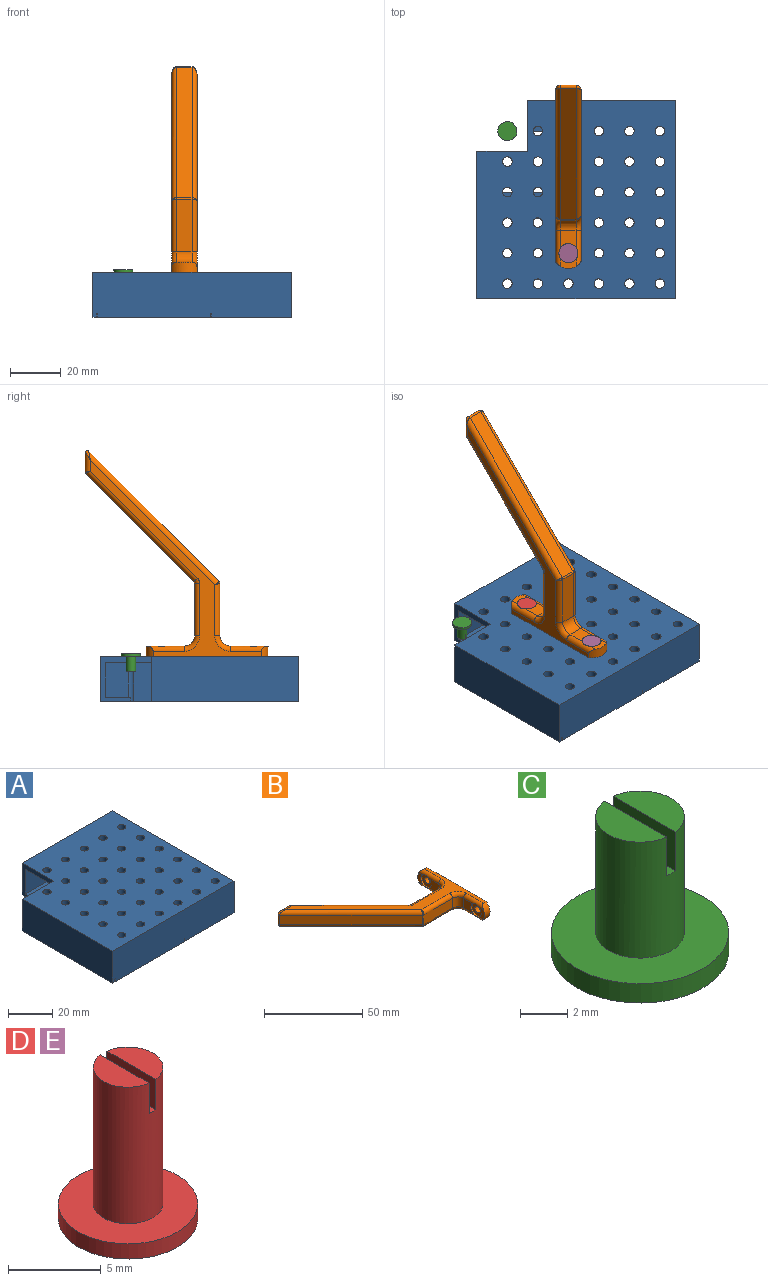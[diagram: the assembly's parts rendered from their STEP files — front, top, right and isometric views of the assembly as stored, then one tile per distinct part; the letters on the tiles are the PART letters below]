
ASSEMBLY  parts=5 mates=4
PART A: 73 faces, bbox 78x78x17.8 mm
  f0: plane 11.33x1.5mm, normal (1,0,0), area 17mm2, adj f6,f15,f25,f26,f48
  f1: plane 10.65x1.5mm, normal (1,0,0), area 16mm2, adj f6,f14,f46,f48
  f2: plane 10.65x1.5mm, normal (1,0,0), area 16mm2, adj f6,f17,f46,f47
  f3: plane 5.33x1.5mm, normal (1,0,0), area 8mm2, adj f6,f16,f45,f47
  f4: plane 45x44mm, normal (0,0,-1), area 1556.9mm2, adj f7,f8,f9,f13,f24,f28,f29,f30
  f5: plane 78x31.5mm, normal (0,0,-1), area 2261.6mm2, adj f7,f8,f9,f10,f11,f12,f13,f27
  f6: plane 44.5x42mm, normal (0,0,-1), area 1769.3mm2, adj f0,f1,f2,f3,f25,f39,f45,f46
  f7: plane 15.25x9.75mm, normal (-1,0,0), area 148.7mm2, adj f4,f5,f50,f51
  f8: plane 15.25x9.75mm, normal (-1,0,0), area 136.7mm2, adj f4,f5,f15,f37,f48,f51
  f9: plane 15.25x9.75mm, normal (-1,0,0), area 148.7mm2, adj f4,f5,f49,f50
  f10: plane 9.75x1.5mm, normal (-1,0,0), area 14.6mm2, adj f5,f14,f46,f48
  f11: plane 9.75x1.5mm, normal (-1,0,0), area 14.6mm2, adj f5,f17,f46,f47
  f12: plane 4.88x1.5mm, normal (-1,0,0), area 7.3mm2, adj f5,f16,f45,f47
  f13: plane 15.25x10.88mm, normal (-1,0,0), area 138.3mm2, adj f4,f5,f24,f27,f41,f49
  f14: plane 10.65x0.25mm, normal (0,0,-1), area 2.5mm2, adj f1,f10,f46,f48
  f15: plane 1.33x0.25mm, normal (0,0,-1), area 0.3mm2, adj f0,f8,f37,f48
  f16: plane 5.33x0.25mm, normal (0,0,-1), area 1.3mm2, adj f3,f12,f45,f47
  f17: plane 10.65x0.25mm, normal (0,0,-1), area 2.5mm2, adj f2,f11,f46,f47
  f18: plane 58x1.5mm, normal (0,0,-1), area 87mm2, adj f20,f36,f43,f45
  f19: plane 26.25x12mm, normal (0,0,-1), area 315mm2, adj f21,f27,f40,f42
  f20: plane 58x17.75mm, normal (-1,0,0), area 1029.5mm2, adj f18,f23,f43,f45
  f21: plane 26.25x1.5mm, normal (0,-1,0), area 39.4mm2, adj f19,f22,f40,f42
  f22: plane 26.25x10mm, normal (0,0,1), area 262.5mm2, adj f21,f24,f40,f42
  f23: plane 78x78mm, normal (0,0,1), area 5297.4mm2, adj f20,f27,f28,f29,f30,f31,f32,f33
  f24: plane 26.5x13.75mm, normal (0,-1,0), area 364.4mm2, adj f4,f13,f22,f41,f42
  f25: plane 44.5x1.5mm, normal (0,1,0), area 66.7mm2, adj f0,f6,f26,f39
  f26: plane 44.5x10mm, normal (0,0,1), area 445mm2, adj f0,f25,f37,f39
  f27: plane 58x17.75mm, normal (0,1,0), area 1029.1mm2, adj f5,f13,f19,f23,f40,f41,f42,f44
  f28: cylinder r=1.88mm len=3.75mm, axis (0,0,-1), area 29.5mm2, adj f4,f23
  f29: cylinder r=1.88mm len=3.75mm, axis (0,0,-1), area 29.5mm2, adj f4,f23
  f30: cylinder r=1.88mm len=3.75mm, axis (0,0,-1), area 29.5mm2, adj f4,f23
  f31: cylinder r=1.88mm len=3.75mm, axis (0,0,-1), area 29.5mm2, adj f4,f23
  f32: cylinder r=1.88mm len=3.75mm, axis (0,0,-1), area 29.5mm2, adj f4,f23
  f33: cylinder r=1.88mm len=3.75mm, axis (0,0,-1), area 29.5mm2, adj f4,f23
  f34: cylinder r=1.88mm len=3.75mm, axis (0,0,-1), area 29.5mm2, adj f4,f23
  f35: cylinder r=1.88mm len=3.75mm, axis (0,0,-1), area 29.5mm2, adj f4,f23
  f36: plane 58x15.25mm, normal (1,0,0), area 444.5mm2, adj f4,f18,f37,f38,f43,f45
  f37: plane 45x13.75mm, normal (0,1,0), area 618.8mm2, adj f4,f8,f15,f26,f36,f38
  f38: plane 32x0.25mm, normal (0,0,-1), area 8mm2, adj f36,f37,f39,f45
  f39: plane 42x1.5mm, normal (-1,0,0), area 63mm2, adj f6,f25,f26,f38,f45
  f40: plane 12x1.5mm, normal (1,0,0), area 18mm2, adj f19,f21,f22,f27,f41
  f41: plane 2x0.25mm, normal (0,0,-1), area 0.5mm2, adj f13,f24,f27,f40
  f42: plane 20x17.75mm, normal (-1,0,0), area 95.5mm2, adj f4,f19,f21,f22,f23,f24,f27,f43
  f43: plane 20x17.75mm, normal (0,1,0), area 72.9mm2, adj f4,f18,f20,f23,f36,f42
  f44: plane 78x17.75mm, normal (1,0,0), area 1384.5mm2, adj f5,f23,f27,f45
  f45: plane 78x17.75mm, normal (0,-1,0), area 1383.8mm2, adj f3,f5,f6,f12,f16,f18,f20,f23
  f46: cylinder r=1.88mm len=17.75mm, axis (0,0,1), area 207.6mm2, adj f1,f2,f5,f6,f10,f11,f14,f17
  f47: cylinder r=1.88mm len=17.75mm, axis (0,0,1), area 207.6mm2, adj f2,f3,f5,f6,f11,f12,f16,f17
  f48: cylinder r=1.88mm len=17.75mm, axis (0,0,1), area 207.6mm2, adj f0,f1,f5,f6,f8,f10,f14,f15
  f49: cylinder r=1.88mm len=17.75mm, axis (0,0,1), area 172.3mm2, adj f4,f5,f9,f13,f23
  f50: cylinder r=1.88mm len=17.75mm, axis (0,0,1), area 172.3mm2, adj f4,f5,f7,f9,f23
  f51: cylinder r=1.88mm len=17.75mm, axis (0,0,1), area 172.3mm2, adj f4,f5,f7,f8,f23
  f52: cylinder r=1.88mm len=17.75mm, axis (0,0,1), area 209.1mm2, adj f6,f23
  f53: cylinder r=1.88mm len=17.75mm, axis (0,0,1), area 209.1mm2, adj f6,f23
  f54: cylinder r=1.88mm len=17.75mm, axis (0,0,1), area 209.1mm2, adj f6,f23
  f55: cylinder r=1.88mm len=17.75mm, axis (0,0,1), area 209.1mm2, adj f6,f23
  f56: cylinder r=1.88mm len=17.75mm, axis (0,0,1), area 209.1mm2, adj f6,f23
  f57: cylinder r=1.88mm len=17.75mm, axis (0,0,1), area 209.1mm2, adj f6,f23
  f58: cylinder r=1.88mm len=17.75mm, axis (0,0,1), area 209.1mm2, adj f6,f23
  f59: cylinder r=1.88mm len=17.75mm, axis (0,0,1), area 209.1mm2, adj f6,f23
  f60: cylinder r=1.88mm len=17.75mm, axis (0,0,1), area 209.1mm2, adj f6,f23
  f61: cylinder r=1.88mm len=17.75mm, axis (0,0,1), area 209.1mm2, adj f5,f23
  f62: cylinder r=1.88mm len=17.75mm, axis (0,0,1), area 209.1mm2, adj f5,f23
  f63: cylinder r=1.88mm len=17.75mm, axis (0,0,1), area 209.1mm2, adj f5,f23
  f64: cylinder r=1.88mm len=17.75mm, axis (0,0,1), area 209.1mm2, adj f5,f23
  f65: cylinder r=1.88mm len=17.75mm, axis (0,0,1), area 209.1mm2, adj f5,f23
  f66: cylinder r=1.88mm len=17.75mm, axis (0,0,1), area 209.1mm2, adj f5,f23
  f67: cylinder r=1.88mm len=17.75mm, axis (0,0,1), area 209.1mm2, adj f5,f23
  f68: cylinder r=1.88mm len=17.75mm, axis (0,0,1), area 209.1mm2, adj f5,f23
  f69: cylinder r=1.88mm len=17.75mm, axis (0,0,1), area 209.1mm2, adj f5,f23
  f70: cylinder r=1.88mm len=17.75mm, axis (0,0,1), area 209.1mm2, adj f5,f23
  f71: cylinder r=1.88mm len=17.75mm, axis (0,0,1), area 209.1mm2, adj f5,f23
  f72: cylinder r=1.88mm len=17.75mm, axis (0,0,1), area 209.1mm2, adj f5,f23
PART B: 52 faces, bbox 82x72x10 mm
  f0: plane 6.75x6mm, normal (-1,0,0), area 34.2mm2, adj f8,f34,f47,f49
  f1: plane 6x3.75mm, normal (-1,0,0), area 14.6mm2, adj f21,f34,f47,f49
  f2: plane 6x3.75mm, normal (-1,0,0), area 14.6mm2, adj f20,f22,f35,f50
  f3: plane 6.75x6mm, normal (-1,0,0), area 34.2mm2, adj f9,f22,f35,f50
  f4: cylinder r=1.88mm len=3.75mm, axis (1,0,0), area 35.3mm2, adj f6,f48
  f5: plane 77.17x67.32mm, normal (0,0,1), area 462.7mm2, adj f6,f20,f21,f35,f36,f37,f38,f39
  f6: plane 48x10mm, normal (1,0,0), area 442mm2, adj f4,f5,f7,f19,f20,f21
  f7: plane 77.17x67.32mm, normal (0,0,-1), area 462.7mm2, adj f6,f20,f21,f22,f23,f24,f25,f26
  f8: cylinder r=4mm len=6mm, axis (0,0,-1), area 37.7mm2, adj f0,f18,f33,f46
  f9: cylinder r=4mm len=6mm, axis (0,0,-1), area 37.7mm2, adj f3,f10,f23,f36
  f10: plane 20.67x6mm, normal (0,1,0), area 124mm2, adj f9,f11,f24,f37
  f11: cylinder r=0.81mm len=6mm, axis (0,0,-1), area 3.8mm2, adj f10,f12,f25,f38
  f12: plane 42.53x42.53mm, normal (0.71,0.71,0), area 360.9mm2, adj f11,f13,f26,f39
  f13: cylinder r=0.81mm len=6mm, axis (0,0,-1), area 3.8mm2, adj f12,f14,f27,f40
  f14: plane 7.72x6mm, normal (0,1,0), area 46.3mm2, adj f13,f15,f28,f41
  f15: cylinder r=0.81mm len=6mm, axis (0,0,-1), area 11.4mm2, adj f14,f16,f29,f42
  f16: plane 51.33x51.33mm, normal (-0.71,-0.71,0), area 435.6mm2, adj f15,f17,f30,f43
  f17: cylinder r=1mm len=6mm, axis (0,0,-1), area 4.7mm2, adj f16,f18,f31,f44
  f18: plane 20.59x6mm, normal (0,-1,0), area 123.5mm2, adj f8,f17,f32,f45
  f19: cylinder r=1.88mm len=3.75mm, axis (1,0,0), area 35.3mm2, adj f6,f51
  f20: cylinder r=6mm len=10mm, axis (1,0,0), area 44.6mm2, adj f2,f5,f6,f7,f22,f35
  f21: cylinder r=6mm len=10mm, axis (1,0,0), area 44.6mm2, adj f1,f5,f6,f7,f34,f47
  f22: cylinder r=2mm len=14.2mm, axis (0,-1,0), area 38.9mm2, adj f2,f3,f7,f20,f23,f50
  f23: torus R=6mm, axis (0,0,1), area 23.3mm2, adj f7,f9,f22,f24
  f24: cylinder r=2mm len=20.67mm, axis (-1,0,0), area 64.9mm2, adj f7,f10,f23,f25
  f25: torus R=2.81mm, axis (0,0,1), area 3.8mm2, adj f7,f11,f24,f26
  f26: cylinder r=2mm len=43.94mm, axis (-0.71,0.71,0), area 188.4mm2, adj f7,f12,f25,f27
  f27: bspline ~2.28x2mm, area 1.3mm2, adj f13,f26,f28
  f28: cylinder r=2mm len=7.72mm, axis (-1,0,0), area 20.4mm2, adj f7,f14,f27,f29
  f29: bspline ~4.83x2.82mm, area 4.8mm2, adj f15,f28,f30
  f30: cylinder r=2mm len=52.75mm, axis (0.71,-0.71,0), area 224.3mm2, adj f7,f16,f29,f31
  f31: bspline ~2.28x2mm, area 1.6mm2, adj f17,f30,f32
  f32: cylinder r=2mm len=20.59mm, axis (1,0,0), area 64.2mm2, adj f7,f18,f31,f33
  f33: torus R=6mm, axis (0,0,1), area 23.3mm2, adj f7,f8,f32,f34
  f34: cylinder r=2mm len=14.2mm, axis (0,-1,0), area 38.9mm2, adj f0,f1,f7,f21,f33,f49
  f35: cylinder r=2mm len=14.2mm, axis (0,1,0), area 38.9mm2, adj f2,f3,f5,f20,f36,f50
  f36: torus R=6mm, axis (0,0,1), area 23.3mm2, adj f5,f9,f35,f37
  f37: cylinder r=2mm len=20.67mm, axis (1,0,0), area 64.9mm2, adj f5,f10,f36,f38
  f38: torus R=2.81mm, axis (0,0,1), area 3.8mm2, adj f5,f11,f37,f39
  f39: cylinder r=2mm len=43.94mm, axis (0.71,-0.71,0), area 188.4mm2, adj f5,f12,f38,f40
  f40: bspline ~2.28x2mm, area 1.3mm2, adj f13,f39,f41
  f41: cylinder r=2mm len=7.72mm, axis (1,0,0), area 20.4mm2, adj f5,f14,f40,f42
  f42: bspline ~4.83x2.82mm, area 4.8mm2, adj f15,f41,f43
  f43: cylinder r=2mm len=52.75mm, axis (-0.71,0.71,0), area 224.3mm2, adj f5,f16,f42,f44
  f44: bspline ~2.28x2mm, area 1.6mm2, adj f17,f43,f45
  f45: cylinder r=2mm len=20.59mm, axis (-1,0,0), area 64.2mm2, adj f5,f18,f44,f46
  f46: torus R=6mm, axis (0,0,1), area 23.3mm2, adj f5,f8,f45,f47
  f47: cylinder r=2mm len=14.2mm, axis (0,1,0), area 38.9mm2, adj f0,f1,f5,f21,f46,f49
  f48: plane 7.5x7.5mm, normal (-1,0,0), area 33.1mm2, adj f4,f49
  f49: cylinder r=3.75mm len=7.5mm, axis (-1,0,0), area 22.8mm2, adj f0,f1,f34,f47,f48
  f50: cylinder r=3.75mm len=7.5mm, axis (-1,0,0), area 22.8mm2, adj f2,f3,f22,f35,f51
  f51: plane 7.5x7.5mm, normal (-1,0,0), area 33.1mm2, adj f19,f50
PART C: 9 faces, bbox 7.5x7.5x7 mm
  f0: plane 3.72x1.63mm, normal (0,0,1), area 4.6mm2, adj f1,f7
  f1: cylinder r=1.88mm len=6mm, axis (0,0,-1), area 68.7mm2, adj f0,f2,f4,f6,f7,f8
  f2: plane 3.72x1.63mm, normal (0,0,1), area 4.6mm2, adj f1,f6
  f3: cylinder r=3.75mm len=7.5mm, axis (0,0,-1), area 23.6mm2, adj f4,f5
  f4: plane 7.5x7.5mm, normal (0,0,1), area 33.1mm2, adj f1,f3
  f5: plane 7.5x7.5mm, normal (0,0,-1), area 44.2mm2, adj f3
  f6: plane 3.72x2mm, normal (-1,0,0), area 7.4mm2, adj f1,f2,f8
  f7: plane 3.72x2mm, normal (1,0,0), area 7.4mm2, adj f0,f1,f8
  f8: plane 3.75x0.5mm, normal (0,0,1), area 1.9mm2, adj f1,f6,f7
PART D: 9 faces, bbox 7.5x7.5x10 mm
  f0: plane 3.72x1.63mm, normal (0,0,1), area 4.6mm2, adj f1,f7
  f1: cylinder r=1.88mm len=9mm, axis (0,0,-1), area 104mm2, adj f0,f2,f4,f6,f7,f8
  f2: plane 3.72x1.63mm, normal (0,0,1), area 4.6mm2, adj f1,f6
  f3: cylinder r=3.75mm len=7.5mm, axis (0,0,-1), area 23.6mm2, adj f4,f5
  f4: plane 7.5x7.5mm, normal (0,0,1), area 33.1mm2, adj f1,f3
  f5: plane 7.5x7.5mm, normal (0,0,-1), area 44.2mm2, adj f3
  f6: plane 3.72x2mm, normal (-1,0,0), area 7.4mm2, adj f1,f2,f8
  f7: plane 3.72x2mm, normal (1,0,0), area 7.4mm2, adj f0,f1,f8
  f8: plane 3.75x0.5mm, normal (0,0,1), area 1.9mm2, adj f1,f6,f7
PART E: same geometry as D
PLACE A t=(-24.21,-14.2,-4.44)mm
PLACE B rot(axis=(0,1,0),90deg) t=(-12.21,-32.2,29.81)mm
PLACE C rot(axis=(0,1,0),180deg) t=(-36.21,-2.2,14.31)mm
PLACE D rot(axis=(0,1,0),180deg) t=(-12.21,-14.2,17.31)mm
PLACE E rot(axis=(1,0,0),180deg) t=(-12.21,-50.2,17.31)mm
MATE fastened D.f1 <-> B.f19  axis (0,0,1) through (-12.21,-14.2,16.31)mm
MATE fastened E.f1 <-> B.f49  axis (0,0,1) through (-12.21,-50.2,16.31)mm
MATE fastened C.f1 <-> A.f23  axis (0,0,1) through (-36.21,-2.2,13.31)mm
MATE fastened B.f19 <-> A.f35  axis (0,0,-1) through (-12.21,-14.2,13.31)mm
